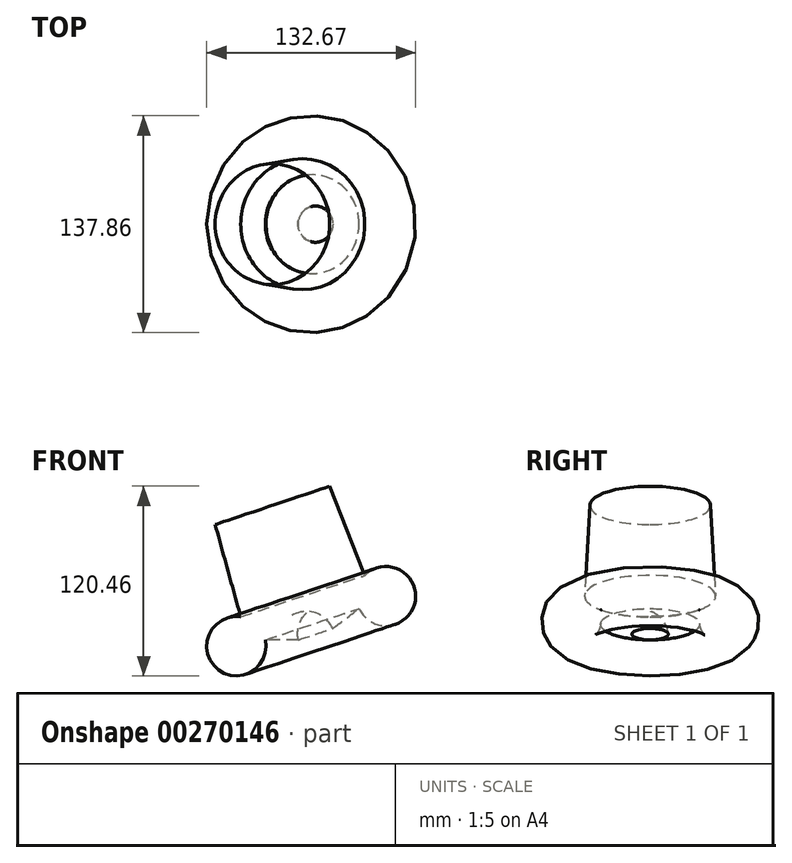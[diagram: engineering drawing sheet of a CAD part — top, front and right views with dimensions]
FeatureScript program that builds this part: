
annotation { "Feature Type Name" : "Feature", "Feature Type Description" : "" }
export const myFeature = defineFeature(function(context is Context, id is Id, definition is map)
    precondition{}
    {
        {
            var Q0;
            Q0=qCreatedBy(makeId("Front.planeOp"),FACE);
            var sketch = newSketch(context, id + "F0", { "sketchPlane" : qUnion([Q0])});
            skCircle(sketch, "E0", {"center": v(-41.56, 0) * mm, "radius": 18.82 * mm});
            skCircle(sketch, "E1", {"center": v(15.68, 8.02) * mm, "radius": 18.33 * mm});
            skLineSegment(sketch, "E2", {"start": v(-38.8, 18.61) * mm, "end": v(-55.04, 77.28) * mm});
            skLineSegment(sketch, "E3", {"start": v(3.9, 22.07) * mm, "end": v(-14.58, 77.28) * mm});
            skArc(sketch, "E4", {"start": v(-14.58, 77.28) * mm, "mid": v(-34.81, 91.84) * mm, "end": v(-55.04, 77.28) * mm});
            skLineSegment(sketch, "E5", {"start": v(-23.17, 4) * mm, "end": v(-2.2, 4) * mm});
            skSolve(sketch);
        }
        {
            var Q0;
            {var subQ1=sQuery(id+"F0.wireOp",EDGE,"E2");Q0=makeQuery(id+"F0.imprint","IMPRINT",FACE,{"disambiguationData":[TD([[makeQuery(id+"F0.imprint","IMPRINT",EDGE,{"derivedFrom":subQ1}),-1.0]])]});}
            var Q1;
            Q1=sQuery(id+"F0.wireOp",EDGE,"E3");
            revolve(context, id + "F1", {"entities" : qUnion([Q0]), "axis" : qUnion([Q1]), "revolveType" : RevolveType.FULL});
        }
        {
            var Q0;
            {var subQ0=sQuery(id+"F0.wireOp",EDGE,"E0");var subQ1=makeQuery(id+"F0.imprint","INTERSECT",VERTEX,{"derivedFrom":[subQ0,sQuery(id+"F0.wireOp",EDGE,"E2")]});Q0=makeQuery(id+"F0.imprint","IMPRINT",FACE,{"disambiguationData":[TD([[makeQuery(id+"F0.imprint","IMPRINT",EDGE,{"disambiguationData":[TD([[subQ1,1.0]])],"derivedFrom":subQ0}),1.0]])]});}
            var Q1;
            Q1=makeQuery(id+"F1.opRevolve","SWEPT_FACE",FACE,{"disambiguationData":[OSD([sQuery(id+"F0.wireOp",EDGE,"E0")])]});
            revolve(context, id + "F2", {"operationType" : NewBodyOperationType.ADD, "entities" : qUnion([Q0]), "axis" : qUnion([Q1]), "revolveType" : RevolveType.FULL});
        }
    });
